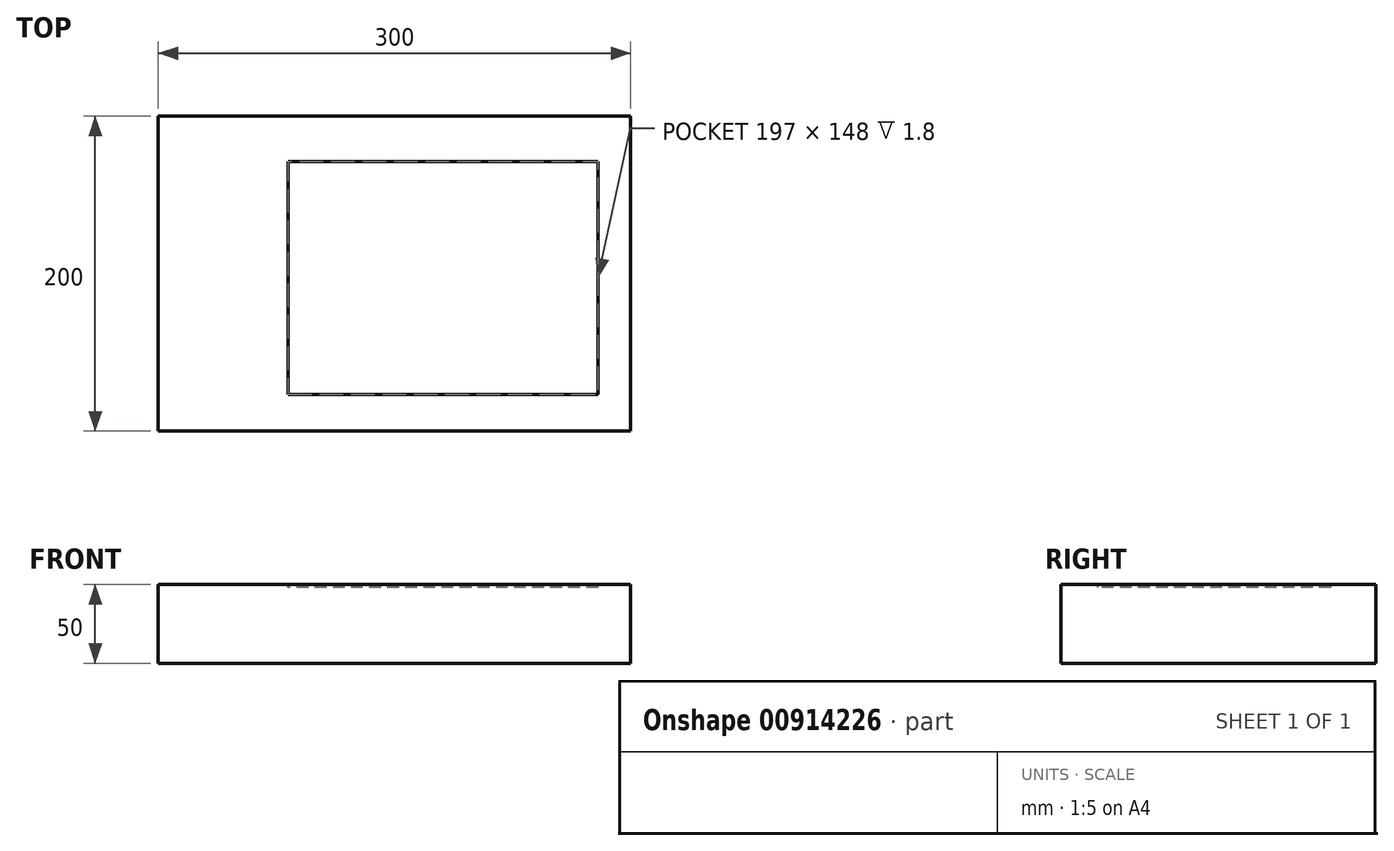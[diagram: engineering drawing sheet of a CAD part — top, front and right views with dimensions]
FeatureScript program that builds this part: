
annotation { "Feature Type Name" : "Feature", "Feature Type Description" : "" }
export const myFeature = defineFeature(function(context is Context, id is Id, definition is map)
    precondition{}
    {
        {
            var Q0;
            Q0=qCreatedBy(makeId("Top.planeOp"),FACE);
            var sketch = newSketch(context, id + "F0", { "sketchPlane" : qUnion([Q0])});
            skLineSegment(sketch, "E0.bottom", {"start": v(150, -100) * mm, "end": v(-150, -100) * mm});
            skLineSegment(sketch, "E0.top", {"start": v(150, 100) * mm, "end": v(-150, 100) * mm});
            skLineSegment(sketch, "E0.left", {"start": v(150, -100) * mm, "end": v(150, 100) * mm});
            skLineSegment(sketch, "E0.right", {"start": v(-150, -100) * mm, "end": v(-150, 100) * mm});
            skPoint(sketch, "E0.middle", {"position": v(0, 0) * mm});
            skSolve(sketch);
        }
        {
            var Q0;
            Q0=makeQuery(id+"F0.imprint","IMPRINT",FACE,{"disambiguationData":[TD([[makeQuery(id+"F0.imprint","IMPRINT",EDGE,{"derivedFrom":sQuery(id+"F0.wireOp",EDGE,"E0.bottom")}),-1.0]])]});
            extrude(context, id + "F1", {"entities" : qUnion([Q0]), "oppositeDirection" : true, "depth" : 50 * mm, "offsetDistance" : 25 * mm});
        }
        {
            var Q0;
            Q0=makeQuery(id+"F1.opExtrude","CAP_FACE",FACE,{"disambiguationData":[OSD([sQuery(id+"F0.wireOp",EDGE,"E0.bottom"),sQuery(id+"F0.wireOp",EDGE,"E0.top"),sQuery(id+"F0.wireOp",EDGE,"E0.left"),sQuery(id+"F0.wireOp",EDGE,"E0.right")])],"isStart":true});
            var sketch = newSketch(context, id + "F2", { "sketchPlane" : qUnion([Q0])});
            skLineSegment(sketch, "E1.bottom", {"start": v(129.34, 71.24) * mm, "end": v(-67.66, 71.24) * mm});
            skLineSegment(sketch, "E1.top", {"start": v(129.34, -76.76) * mm, "end": v(-67.66, -76.76) * mm});
            skLineSegment(sketch, "E1.left", {"start": v(129.34, 71.24) * mm, "end": v(129.34, -76.76) * mm});
            skLineSegment(sketch, "E1.right", {"start": v(-67.66, 71.24) * mm, "end": v(-67.66, -76.76) * mm});
            skSolve(sketch);
        }
        {
            var Q0;
            Q0 = qSketchRegion(id + "F2", true);
            extrude(context, id + "F3", {"entities" : qUnion([Q0]), "operationType" : NewBodyOperationType.REMOVE, "oppositeDirection" : true, "depth" : 1.8 * mm, "offsetDistance" : 25 * mm});
        }
    });
